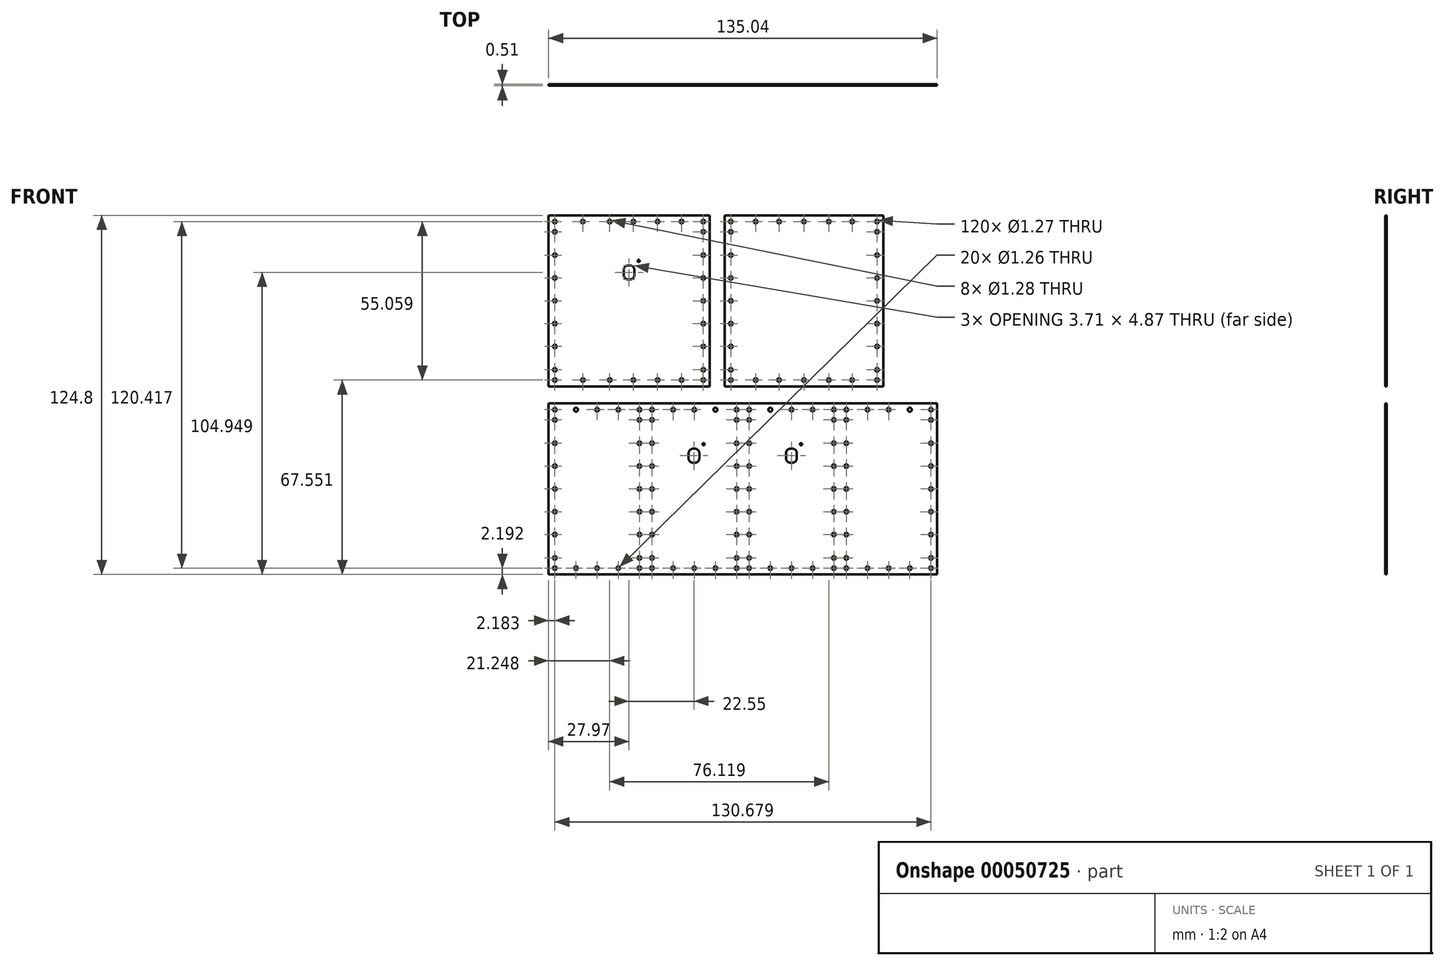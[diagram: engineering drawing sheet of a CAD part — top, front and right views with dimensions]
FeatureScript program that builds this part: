
annotation { "Feature Type Name" : "Feature", "Feature Type Description" : "" }
export const myFeature = defineFeature(function(context is Context, id is Id, definition is map)
    precondition{}
    {
        {
            var Q0;
            Q0=qCreatedBy(makeId("Front.planeOp"),FACE);
            var sketch = newSketch(context, id + "F0", { "sketchPlane" : qUnion([Q0])});
            skLineSegment(sketch, "E0", {"start": v(-27.97, 29.72) * mm, "end": v(-27.97, -29.72) * mm});
            skLineSegment(sketch, "E1", {"start": v(-27.97, -29.72) * mm, "end": v(27.97, -29.72) * mm});
            skLineSegment(sketch, "E2", {"start": v(27.97, -29.72) * mm, "end": v(27.97, 29.72) * mm});
            skCircle(sketch, "E3", {"center": v(-25.79, 27.53) * mm, "radius": 0.63 * mm});
            skLineSegment(sketch, "E4", {"start": v(-27.97, 29.72) * mm, "end": v(27.97, 29.72) * mm});
            skCircle(sketch, "E5.MirrorC", {"center": v(25.79, 27.53) * mm, "radius": 0.63 * mm});
            skCircle(sketch, "E6.MirrorC", {"center": v(-25.79, -27.53) * mm, "radius": 0.63 * mm});
            skCircle(sketch, "E7.MirrorC", {"center": v(25.79, -27.53) * mm, "radius": 0.63 * mm});
            skCircle(sketch, "E8", {"center": v(-25.79, 0) * mm, "radius": 0.63 * mm});
            skCircle(sketch, "E9.MirrorC", {"center": v(25.79, 0) * mm, "radius": 0.63 * mm});
            skCircle(sketch, "E10", {"center": v(-25.79, 23.98) * mm, "radius": 0.63 * mm});
            skCircle(sketch, "E11.MirrorC", {"center": v(-25.79, -23.98) * mm, "radius": 0.63 * mm});
            skCircle(sketch, "E12.MirrorC", {"center": v(25.79, 23.98) * mm, "radius": 0.63 * mm});
            skCircle(sketch, "E13.MirrorC", {"center": v(25.79, -23.98) * mm, "radius": 0.63 * mm});
            skCircle(sketch, "E14", {"center": v(-25.79, 15.86) * mm, "radius": 0.64 * mm});
            skCircle(sketch, "E15", {"center": v(-25.79, 7.93) * mm, "radius": 0.64 * mm});
            skCircle(sketch, "E16.MirrorC", {"center": v(-25.79, -15.86) * mm, "radius": 0.64 * mm});
            skCircle(sketch, "E17.MirrorC", {"center": v(-25.79, -7.93) * mm, "radius": 0.64 * mm});
            skCircle(sketch, "E18.MirrorC", {"center": v(25.79, 15.86) * mm, "radius": 0.64 * mm});
            skCircle(sketch, "E19.MirrorC", {"center": v(25.79, 7.93) * mm, "radius": 0.64 * mm});
            skCircle(sketch, "E20.MirrorC", {"center": v(25.79, -7.93) * mm, "radius": 0.64 * mm});
            skCircle(sketch, "E21.MirrorC", {"center": v(25.79, -15.86) * mm, "radius": 0.64 * mm});
            skCircle(sketch, "E22", {"center": v(-16.05, 27.53) * mm, "radius": 0.63 * mm});
            skCircle(sketch, "E23", {"center": v(-6.72, 27.53) * mm, "radius": 0.64 * mm});
            skCircle(sketch, "E24", {"center": v(1.51, 27.53) * mm, "radius": 0.63 * mm});
            skCircle(sketch, "E25", {"center": v(18.24, 27.53) * mm, "radius": 0.64 * mm});
            skCircle(sketch, "E26", {"center": v(9.92, 27.53) * mm, "radius": 0.63 * mm});
            skCircle(sketch, "E27.MirrorC", {"center": v(-16.05, -27.53) * mm, "radius": 0.63 * mm});
            skCircle(sketch, "E28.MirrorC", {"center": v(-6.72, -27.53) * mm, "radius": 0.64 * mm});
            skCircle(sketch, "E29.MirrorC", {"center": v(1.51, -27.53) * mm, "radius": 0.63 * mm});
            skCircle(sketch, "E30.MirrorC", {"center": v(9.92, -27.53) * mm, "radius": 0.63 * mm});
            skCircle(sketch, "E31.MirrorC", {"center": v(18.24, -27.53) * mm, "radius": 0.64 * mm});
            skPoint(sketch, "E32.endSnap0", {"position": v(0, 29.72) * mm});
            skLineSegment(sketch, "E33", {"start": v(1.85, 12.3) * mm, "end": v(1.85, 7.43) * mm});
            skLineSegment(sketch, "E34.MirrorCS", {"start": v(-1.85, 12.3) * mm, "end": v(-1.85, 7.43) * mm});
            skLineSegment(sketch, "E35", {"start": v(1.85, 12.3) * mm, "end": v(-1.85, 12.3) * mm});
            skLineSegment(sketch, "E36", {"start": v(1.85, 7.43) * mm, "end": v(-1.85, 7.43) * mm});
            skCircle(sketch, "E37", {"center": v(3.34, 13.86) * mm, "radius": 0.37 * mm});
            skLineSegment(sketch, "E38.MirrorCS", {"start": v(-27.97, -29.72) * mm, "end": v(-27.97, 29.72) * mm});
            skLineSegment(sketch, "E39.MirrorCS", {"start": v(33.18, -29.72) * mm, "end": v(33.18, 29.72) * mm});
            skLineSegment(sketch, "E40", {"start": v(33.18, 29.72) * mm, "end": v(88.34, 29.72) * mm});
            skLineSegment(sketch, "E41", {"start": v(88.34, 29.72) * mm, "end": v(88.34, -29.72) * mm});
            skLineSegment(sketch, "E42", {"start": v(88.34, -29.72) * mm, "end": v(33.18, -29.72) * mm});
            skCircle(sketch, "E43.MirrorC", {"center": v(35.36, 27.53) * mm, "radius": 0.63 * mm});
            skCircle(sketch, "E44.MirrorC", {"center": v(35.36, 23.98) * mm, "radius": 0.63 * mm});
            skCircle(sketch, "E45.MirrorC", {"center": v(35.36, 15.86) * mm, "radius": 0.64 * mm});
            skCircle(sketch, "E46.MirrorC", {"center": v(35.36, 7.93) * mm, "radius": 0.64 * mm});
            skCircle(sketch, "E47.MirrorC", {"center": v(35.36, 0) * mm, "radius": 0.63 * mm});
            skCircle(sketch, "E48.MirrorC", {"center": v(35.36, -7.93) * mm, "radius": 0.64 * mm});
            skCircle(sketch, "E49.MirrorC", {"center": v(35.36, -15.86) * mm, "radius": 0.64 * mm});
            skCircle(sketch, "E50.MirrorC", {"center": v(35.36, -23.98) * mm, "radius": 0.63 * mm});
            skCircle(sketch, "E51.MirrorC", {"center": v(35.36, -27.53) * mm, "radius": 0.63 * mm});
            skCircle(sketch, "E52.MirrorC", {"center": v(86.16, 27.53) * mm, "radius": 0.63 * mm});
            skCircle(sketch, "E53.MirrorC", {"center": v(86.16, 23.98) * mm, "radius": 0.63 * mm});
            skCircle(sketch, "E54.MirrorC", {"center": v(86.16, 15.86) * mm, "radius": 0.64 * mm});
            skCircle(sketch, "E55.MirrorC", {"center": v(86.16, 7.93) * mm, "radius": 0.64 * mm});
            skCircle(sketch, "E56.MirrorC", {"center": v(86.16, 0) * mm, "radius": 0.63 * mm});
            skCircle(sketch, "E57.MirrorC", {"center": v(86.16, -7.93) * mm, "radius": 0.64 * mm});
            skCircle(sketch, "E58.MirrorC", {"center": v(86.16, -15.86) * mm, "radius": 0.64 * mm});
            skCircle(sketch, "E59.MirrorC", {"center": v(86.16, -23.98) * mm, "radius": 0.63 * mm});
            skCircle(sketch, "E60.MirrorC", {"center": v(86.16, -27.53) * mm, "radius": 0.63 * mm});
            skCircle(sketch, "E61", {"center": v(60.76, 27.53) * mm, "radius": 0.63 * mm});
            skCircle(sketch, "E62", {"center": v(43.99, 27.53) * mm, "radius": 0.64 * mm});
            skCircle(sketch, "E63", {"center": v(52.12, 27.53) * mm, "radius": 0.64 * mm});
            skCircle(sketch, "E64.MirrorC", {"center": v(69.4, 27.53) * mm, "radius": 0.64 * mm});
            skCircle(sketch, "E65.MirrorC", {"center": v(77.53, 27.53) * mm, "radius": 0.64 * mm});
            skCircle(sketch, "E66.MirrorC", {"center": v(43.99, -27.53) * mm, "radius": 0.64 * mm});
            skCircle(sketch, "E67.MirrorC", {"center": v(52.12, -27.53) * mm, "radius": 0.64 * mm});
            skCircle(sketch, "E68.MirrorC", {"center": v(60.76, -27.53) * mm, "radius": 0.63 * mm});
            skCircle(sketch, "E69.MirrorC", {"center": v(69.4, -27.53) * mm, "radius": 0.64 * mm});
            skCircle(sketch, "E70.MirrorC", {"center": v(77.53, -27.53) * mm, "radius": 0.64 * mm});
            skLineSegment(sketch, "E71", {"start": v(-32.87, -32.68) * mm, "end": v(110.1, -32.68) * mm});
            skLineSegment(sketch, "E72.MirrorCS", {"start": v(-27.97, -95.08) * mm, "end": v(-27.97, -35.64) * mm});
            skCircle(sketch, "E73.MirrorC", {"center": v(-25.79, -92.89) * mm, "radius": 0.63 * mm});
            skCircle(sketch, "E74.MirrorC", {"center": v(-25.79, -89.34) * mm, "radius": 0.63 * mm});
            skCircle(sketch, "E75.MirrorC", {"center": v(-25.79, -81.22) * mm, "radius": 0.64 * mm});
            skCircle(sketch, "E76.MirrorC", {"center": v(-25.79, -73.3) * mm, "radius": 0.64 * mm});
            skCircle(sketch, "E77.MirrorC", {"center": v(-25.79, -65.36) * mm, "radius": 0.63 * mm});
            skCircle(sketch, "E78.MirrorC", {"center": v(-25.79, -57.43) * mm, "radius": 0.64 * mm});
            skCircle(sketch, "E79.MirrorC", {"center": v(-25.79, -49.5) * mm, "radius": 0.64 * mm});
            skCircle(sketch, "E80.MirrorC", {"center": v(-25.79, -41.38) * mm, "radius": 0.63 * mm});
            skCircle(sketch, "E81.MirrorC", {"center": v(-25.79, -37.83) * mm, "radius": 0.63 * mm});
            skLineSegment(sketch, "E82", {"start": v(-27.97, -35.64) * mm, "end": v(5.8, -35.64) * mm});
            skLineSegment(sketch, "E83", {"start": v(5.8, -35.64) * mm, "end": v(5.8, -95.08) * mm});
            skLineSegment(sketch, "E84.MirrorCS", {"start": v(39.55, -35.64) * mm, "end": v(5.8, -35.64) * mm});
            skLineSegment(sketch, "E85", {"start": v(39.55, -35.64) * mm, "end": v(39.55, -95.08) * mm});
            skLineSegment(sketch, "E86.MirrorCS", {"start": v(39.55, -35.64) * mm, "end": v(73.31, -35.64) * mm});
            skLineSegment(sketch, "E87", {"start": v(73.31, -35.64) * mm, "end": v(73.31, -95.08) * mm});
            skLineSegment(sketch, "E88.MirrorCS", {"start": v(107.07, -35.64) * mm, "end": v(73.31, -35.64) * mm});
            skLineSegment(sketch, "E89", {"start": v(-27.97, -95.08) * mm, "end": v(5.8, -95.08) * mm});
            skLineSegment(sketch, "E90", {"start": v(5.8, -95.08) * mm, "end": v(39.55, -95.08) * mm});
            skLineSegment(sketch, "E91", {"start": v(39.55, -95.08) * mm, "end": v(73.31, -95.08) * mm});
            skLineSegment(sketch, "E92", {"start": v(73.31, -95.08) * mm, "end": v(107.07, -95.08) * mm});
            skLineSegment(sketch, "E93", {"start": v(107.07, -95.08) * mm, "end": v(107.07, -35.64) * mm});
            skCircle(sketch, "E94.MirrorC", {"center": v(3.62, -37.83) * mm, "radius": 0.63 * mm});
            skCircle(sketch, "E95.MirrorC", {"center": v(3.62, -41.38) * mm, "radius": 0.63 * mm});
            skCircle(sketch, "E96.MirrorC", {"center": v(3.62, -49.5) * mm, "radius": 0.64 * mm});
            skCircle(sketch, "E97.MirrorC", {"center": v(3.62, -57.43) * mm, "radius": 0.64 * mm});
            skCircle(sketch, "E98.MirrorC", {"center": v(3.62, -65.36) * mm, "radius": 0.63 * mm});
            skCircle(sketch, "E99.MirrorC", {"center": v(3.62, -73.3) * mm, "radius": 0.64 * mm});
            skCircle(sketch, "E100.MirrorC", {"center": v(3.62, -81.22) * mm, "radius": 0.64 * mm});
            skCircle(sketch, "E101.MirrorC", {"center": v(3.62, -89.34) * mm, "radius": 0.63 * mm});
            skCircle(sketch, "E102.MirrorC", {"center": v(3.62, -92.89) * mm, "radius": 0.63 * mm});
            skCircle(sketch, "E103.MirrorC", {"center": v(7.97, -37.83) * mm, "radius": 0.63 * mm});
            skCircle(sketch, "E104.MirrorC", {"center": v(7.97, -41.38) * mm, "radius": 0.63 * mm});
            skCircle(sketch, "E105.MirrorC", {"center": v(7.97, -49.5) * mm, "radius": 0.64 * mm});
            skCircle(sketch, "E106.MirrorC", {"center": v(7.97, -57.43) * mm, "radius": 0.64 * mm});
            skCircle(sketch, "E107.MirrorC", {"center": v(7.97, -65.36) * mm, "radius": 0.63 * mm});
            skCircle(sketch, "E108.MirrorC", {"center": v(7.97, -73.3) * mm, "radius": 0.64 * mm});
            skCircle(sketch, "E109.MirrorC", {"center": v(7.97, -81.22) * mm, "radius": 0.64 * mm});
            skCircle(sketch, "E110.MirrorC", {"center": v(7.97, -89.34) * mm, "radius": 0.63 * mm});
            skCircle(sketch, "E111.MirrorC", {"center": v(7.97, -92.89) * mm, "radius": 0.63 * mm});
            skCircle(sketch, "E112.MirrorC", {"center": v(37.37, -37.83) * mm, "radius": 0.63 * mm});
            skCircle(sketch, "E113.MirrorC", {"center": v(37.37, -41.38) * mm, "radius": 0.63 * mm});
            skCircle(sketch, "E114.MirrorC", {"center": v(37.37, -49.5) * mm, "radius": 0.64 * mm});
            skCircle(sketch, "E115.MirrorC", {"center": v(37.37, -57.43) * mm, "radius": 0.64 * mm});
            skCircle(sketch, "E116.MirrorC", {"center": v(37.37, -65.36) * mm, "radius": 0.63 * mm});
            skCircle(sketch, "E117.MirrorC", {"center": v(37.37, -73.3) * mm, "radius": 0.64 * mm});
            skCircle(sketch, "E118.MirrorC", {"center": v(37.37, -81.22) * mm, "radius": 0.64 * mm});
            skCircle(sketch, "E119.MirrorC", {"center": v(37.37, -89.34) * mm, "radius": 0.63 * mm});
            skCircle(sketch, "E120.MirrorC", {"center": v(37.37, -92.89) * mm, "radius": 0.63 * mm});
            skCircle(sketch, "E121.MirrorC", {"center": v(41.73, -37.83) * mm, "radius": 0.63 * mm});
            skCircle(sketch, "E122.MirrorC", {"center": v(41.73, -41.38) * mm, "radius": 0.63 * mm});
            skCircle(sketch, "E123.MirrorC", {"center": v(41.73, -49.5) * mm, "radius": 0.64 * mm});
            skCircle(sketch, "E124.MirrorC", {"center": v(41.73, -57.43) * mm, "radius": 0.64 * mm});
            skCircle(sketch, "E125.MirrorC", {"center": v(41.73, -65.36) * mm, "radius": 0.63 * mm});
            skCircle(sketch, "E126.MirrorC", {"center": v(41.73, -73.3) * mm, "radius": 0.64 * mm});
            skCircle(sketch, "E127.MirrorC", {"center": v(41.73, -81.22) * mm, "radius": 0.64 * mm});
            skCircle(sketch, "E128.MirrorC", {"center": v(41.73, -89.34) * mm, "radius": 0.63 * mm});
            skCircle(sketch, "E129.MirrorC", {"center": v(41.73, -92.89) * mm, "radius": 0.63 * mm});
            skCircle(sketch, "E130.MirrorC", {"center": v(71.13, -37.83) * mm, "radius": 0.63 * mm});
            skCircle(sketch, "E131.MirrorC", {"center": v(71.13, -41.38) * mm, "radius": 0.63 * mm});
            skCircle(sketch, "E132.MirrorC", {"center": v(71.13, -49.5) * mm, "radius": 0.64 * mm});
            skCircle(sketch, "E133.MirrorC", {"center": v(71.13, -57.43) * mm, "radius": 0.64 * mm});
            skCircle(sketch, "E134.MirrorC", {"center": v(71.13, -65.36) * mm, "radius": 0.63 * mm});
            skCircle(sketch, "E135.MirrorC", {"center": v(71.13, -73.3) * mm, "radius": 0.64 * mm});
            skCircle(sketch, "E136.MirrorC", {"center": v(71.13, -81.22) * mm, "radius": 0.64 * mm});
            skCircle(sketch, "E137.MirrorC", {"center": v(71.13, -89.34) * mm, "radius": 0.63 * mm});
            skCircle(sketch, "E138.MirrorC", {"center": v(71.13, -92.89) * mm, "radius": 0.63 * mm});
            skCircle(sketch, "E139.MirrorC", {"center": v(75.5, -37.83) * mm, "radius": 0.63 * mm});
            skCircle(sketch, "E140.MirrorC", {"center": v(75.5, -41.38) * mm, "radius": 0.63 * mm});
            skCircle(sketch, "E141.MirrorC", {"center": v(75.5, -49.5) * mm, "radius": 0.64 * mm});
            skCircle(sketch, "E142.MirrorC", {"center": v(75.5, -57.43) * mm, "radius": 0.64 * mm});
            skCircle(sketch, "E143.MirrorC", {"center": v(75.5, -65.36) * mm, "radius": 0.63 * mm});
            skCircle(sketch, "E144.MirrorC", {"center": v(75.5, -73.3) * mm, "radius": 0.64 * mm});
            skCircle(sketch, "E145.MirrorC", {"center": v(75.5, -81.22) * mm, "radius": 0.64 * mm});
            skCircle(sketch, "E146.MirrorC", {"center": v(75.5, -89.34) * mm, "radius": 0.63 * mm});
            skCircle(sketch, "E147.MirrorC", {"center": v(75.5, -92.89) * mm, "radius": 0.63 * mm});
            skCircle(sketch, "E148.MirrorC", {"center": v(104.9, -37.83) * mm, "radius": 0.63 * mm});
            skCircle(sketch, "E149.MirrorC", {"center": v(104.9, -41.38) * mm, "radius": 0.63 * mm});
            skCircle(sketch, "E150.MirrorC", {"center": v(104.9, -49.5) * mm, "radius": 0.64 * mm});
            skCircle(sketch, "E151.MirrorC", {"center": v(104.9, -57.43) * mm, "radius": 0.64 * mm});
            skCircle(sketch, "E152.MirrorC", {"center": v(104.9, -65.36) * mm, "radius": 0.63 * mm});
            skCircle(sketch, "E153.MirrorC", {"center": v(104.9, -73.3) * mm, "radius": 0.64 * mm});
            skCircle(sketch, "E154.MirrorC", {"center": v(104.9, -81.22) * mm, "radius": 0.64 * mm});
            skCircle(sketch, "E155.MirrorC", {"center": v(104.9, -89.34) * mm, "radius": 0.63 * mm});
            skCircle(sketch, "E156.MirrorC", {"center": v(104.9, -92.89) * mm, "radius": 0.63 * mm});
            skCircle(sketch, "E157", {"center": v(-11.09, -37.83) * mm, "radius": 0.64 * mm});
            skCircle(sketch, "E158", {"center": v(-11.09, -92.89) * mm, "radius": 0.63 * mm});
            skCircle(sketch, "E159", {"center": v(-18.44, -37.83) * mm, "radius": 0.69 * mm});
            skCircle(sketch, "E160", {"center": v(-3.74, -37.83) * mm, "radius": 0.63 * mm});
            skCircle(sketch, "E161", {"center": v(-18.44, -92.89) * mm, "radius": 0.63 * mm});
            skCircle(sketch, "E162", {"center": v(-3.74, -92.89) * mm, "radius": 0.63 * mm});
            skCircle(sketch, "E163.MirrorC", {"center": v(15.32, -37.83) * mm, "radius": 0.63 * mm});
            skCircle(sketch, "E164.MirrorC", {"center": v(22.67, -37.83) * mm, "radius": 0.64 * mm});
            skCircle(sketch, "E165.MirrorC", {"center": v(30.02, -37.83) * mm, "radius": 0.69 * mm});
            skCircle(sketch, "E166.MirrorC", {"center": v(15.32, -92.89) * mm, "radius": 0.63 * mm});
            skCircle(sketch, "E167.MirrorC", {"center": v(22.67, -92.89) * mm, "radius": 0.63 * mm});
            skCircle(sketch, "E168.MirrorC", {"center": v(30.02, -92.89) * mm, "radius": 0.63 * mm});
            skCircle(sketch, "E169.MirrorC", {"center": v(49.08, -37.83) * mm, "radius": 0.69 * mm});
            skCircle(sketch, "E170.MirrorC", {"center": v(56.43, -37.83) * mm, "radius": 0.64 * mm});
            skCircle(sketch, "E171.MirrorC", {"center": v(63.78, -37.83) * mm, "radius": 0.63 * mm});
            skCircle(sketch, "E172.MirrorC", {"center": v(49.08, -92.89) * mm, "radius": 0.63 * mm});
            skCircle(sketch, "E173.MirrorC", {"center": v(56.43, -92.89) * mm, "radius": 0.63 * mm});
            skCircle(sketch, "E174.MirrorC", {"center": v(63.78, -92.89) * mm, "radius": 0.63 * mm});
            skCircle(sketch, "E175.MirrorC", {"center": v(82.84, -37.83) * mm, "radius": 0.63 * mm});
            skCircle(sketch, "E176.MirrorC", {"center": v(90.2, -37.83) * mm, "radius": 0.64 * mm});
            skCircle(sketch, "E177.MirrorC", {"center": v(97.54, -37.83) * mm, "radius": 0.69 * mm});
            skCircle(sketch, "E178.MirrorC", {"center": v(97.54, -92.89) * mm, "radius": 0.63 * mm});
            skCircle(sketch, "E179.MirrorC", {"center": v(90.2, -92.89) * mm, "radius": 0.63 * mm});
            skCircle(sketch, "E180.MirrorC", {"center": v(82.84, -92.89) * mm, "radius": 0.63 * mm});
            skLineSegment(sketch, "E181", {"start": v(24.4, -51.4) * mm, "end": v(24.4, -56.27) * mm});
            skLineSegment(sketch, "E182.MirrorCS", {"start": v(20.7, -51.4) * mm, "end": v(20.7, -56.27) * mm});
            skLineSegment(sketch, "E183", {"start": v(24.4, -51.4) * mm, "end": v(20.7, -51.4) * mm});
            skLineSegment(sketch, "E184", {"start": v(24.4, -56.27) * mm, "end": v(20.7, -56.27) * mm});
            skCircle(sketch, "E185", {"center": v(25.89, -49.84) * mm, "radius": 0.37 * mm});
            skLineSegment(sketch, "E186", {"start": v(58.26, -51.39) * mm, "end": v(58.26, -56.26) * mm});
            skLineSegment(sketch, "E187.MirrorCS", {"start": v(54.55, -51.39) * mm, "end": v(54.55, -56.26) * mm});
            skLineSegment(sketch, "E188", {"start": v(58.26, -51.39) * mm, "end": v(54.55, -51.39) * mm});
            skLineSegment(sketch, "E189", {"start": v(58.26, -56.26) * mm, "end": v(54.55, -56.26) * mm});
            skCircle(sketch, "E190", {"center": v(59.75, -49.83) * mm, "radius": 0.37 * mm});
            skSolve(sketch);
        }
        {
            var Q0;
            Q0=makeQuery(id+"F0.imprint","IMPRINT",FACE,{"disambiguationData":[TD([[makeQuery(id+"F0.imprint","IMPRINT",EDGE,{"derivedFrom":sQuery(id+"F0.wireOp",EDGE,"E1")}),1.0]])]});
            var Q1;
            Q1=makeQuery(id+"F0.imprint","IMPRINT",FACE,{"disambiguationData":[TD([[makeQuery(id+"F0.imprint","IMPRINT",EDGE,{"derivedFrom":sQuery(id+"F0.wireOp",EDGE,"E39.MirrorCS")}),-1.0]])]});
            var Q2;
            Q2=makeQuery(id+"F0.imprint","IMPRINT",FACE,{"disambiguationData":[TD([[makeQuery(id+"F0.imprint","IMPRINT",EDGE,{"derivedFrom":sQuery(id+"F0.wireOp",EDGE,"E72.MirrorCS")}),-1.0]])]});
            var Q3;
            Q3=makeQuery(id+"F0.imprint","IMPRINT",FACE,{"disambiguationData":[TD([[makeQuery(id+"F0.imprint","IMPRINT",EDGE,{"derivedFrom":sQuery(id+"F0.wireOp",EDGE,"E83")}),1.0]])]});
            var Q4;
            Q4=makeQuery(id+"F0.imprint","IMPRINT",FACE,{"disambiguationData":[TD([[makeQuery(id+"F0.imprint","IMPRINT",EDGE,{"derivedFrom":sQuery(id+"F0.wireOp",EDGE,"E85")}),1.0]])]});
            var Q5;
            Q5=makeQuery(id+"F0.imprint","IMPRINT",FACE,{"disambiguationData":[TD([[makeQuery(id+"F0.imprint","IMPRINT",EDGE,{"derivedFrom":sQuery(id+"F0.wireOp",EDGE,"E87")}),1.0]])]});
            extrude(context, id + "F1", {"entities" : qUnion([Q0, Q1, Q2, Q3, Q4, Q5]), "depth" : 0.5 * mm});
        }
        {
            var Q0;
            Q0=makeQuery(id+"F1.opExtrude","SWEPT_EDGE",EDGE,{"disambiguationData":[OSD([sQuery(id+"F0.wireOp",EDGE,"i2R7Pctc-3fyF-2MkM-alVz-WjF7sQXmCHS1"),sQuery(id+"F0.wireOp",EDGE,"RFerJh6O-CARs-Ny35-0G8d-CF1cur4kfl3N")])]});
            var Q1;
            Q1=makeQuery(id+"F1.opExtrude","SWEPT_EDGE",EDGE,{"disambiguationData":[OSD([sQuery(id+"F0.wireOp",EDGE,"RFerJh6O-CARs-Ny35-0G8d-CF1cur4kfl3N"),sQuery(id+"F0.wireOp",EDGE,"E33")])]});
            var Q2;
            Q2=makeQuery(id+"F1.opExtrude","SWEPT_EDGE",EDGE,{"disambiguationData":[OSD([sQuery(id+"F0.wireOp",EDGE,"7ac9011b-8a2d-43da-9be4-0192752afa2e0.MirrorCS"),sQuery(id+"F0.wireOp",EDGE,"E33")])]});
            var Q3;
            Q3=makeQuery(id+"F1.opExtrude","SWEPT_EDGE",EDGE,{"disambiguationData":[OSD([sQuery(id+"F0.wireOp",EDGE,"dBOPFCVm-Xay8-XRaF-brYx-Q8zsq85a7ZVb"),sQuery(id+"F0.wireOp",EDGE,"i2R7Pctc-3fyF-2MkM-alVz-WjF7sQXmCHS1")])]});
            var Q4;
            Q4=makeQuery(id+"F1.opExtrude","SWEPT_EDGE",EDGE,{"disambiguationData":[OSD([sQuery(id+"F0.wireOp",EDGE,"E34.MirrorCS"),sQuery(id+"F0.wireOp",EDGE,"E35")])]});
            var Q5;
            Q5=makeQuery(id+"F1.opExtrude","SWEPT_EDGE",EDGE,{"disambiguationData":[OSD([sQuery(id+"F0.wireOp",EDGE,"E34.MirrorCS"),sQuery(id+"F0.wireOp",EDGE,"E36")])]});
            fillet(context, id + "F2", {"entities" : qUnion([Q0, Q1, Q2, Q3, Q4, Q5]), "radius" : 1.52 * mm, "tangentPropagation" : true, "allowEdgeOverflow" : false});
        }
        {
            var Q0;
            Q0=makeQuery(id+"F1.opExtrude","SWEPT_EDGE",EDGE,{"disambiguationData":[OSD([sQuery(id+"F0.wireOp",EDGE,"E182.MirrorCS"),sQuery(id+"F0.wireOp",EDGE,"E183")])]});
            var Q1;
            Q1=makeQuery(id+"F1.opExtrude","SWEPT_EDGE",EDGE,{"disambiguationData":[OSD([sQuery(id+"F0.wireOp",EDGE,"E187.MirrorCS"),sQuery(id+"F0.wireOp",EDGE,"E188")])]});
            var Q2;
            Q2=makeQuery(id+"F1.opExtrude","SWEPT_EDGE",EDGE,{"disambiguationData":[OSD([sQuery(id+"F0.wireOp",EDGE,"E181"),sQuery(id+"F0.wireOp",EDGE,"E183")])]});
            var Q3;
            Q3=makeQuery(id+"F1.opExtrude","SWEPT_EDGE",EDGE,{"disambiguationData":[OSD([sQuery(id+"F0.wireOp",EDGE,"E186"),sQuery(id+"F0.wireOp",EDGE,"E188")])]});
            var Q4;
            Q4=makeQuery(id+"F1.opExtrude","SWEPT_EDGE",EDGE,{"disambiguationData":[OSD([sQuery(id+"F0.wireOp",EDGE,"E182.MirrorCS"),sQuery(id+"F0.wireOp",EDGE,"E184")])]});
            var Q5;
            Q5=makeQuery(id+"F1.opExtrude","SWEPT_EDGE",EDGE,{"disambiguationData":[OSD([sQuery(id+"F0.wireOp",EDGE,"E187.MirrorCS"),sQuery(id+"F0.wireOp",EDGE,"E189")])]});
            var Q6;
            Q6=makeQuery(id+"F1.opExtrude","SWEPT_EDGE",EDGE,{"disambiguationData":[OSD([sQuery(id+"F0.wireOp",EDGE,"E186"),sQuery(id+"F0.wireOp",EDGE,"E189")])]});
            var Q7;
            Q7=makeQuery(id+"F1.opExtrude","SWEPT_EDGE",EDGE,{"disambiguationData":[OSD([sQuery(id+"F0.wireOp",EDGE,"E181"),sQuery(id+"F0.wireOp",EDGE,"E184")])]});
            fillet(context, id + "F3", {"entities" : qUnion([Q0, Q1, Q2, Q3, Q4, Q5, Q6, Q7]), "radius" : 1.52 * mm, "tangentPropagation" : true, "allowEdgeOverflow" : false});
        }
    });
